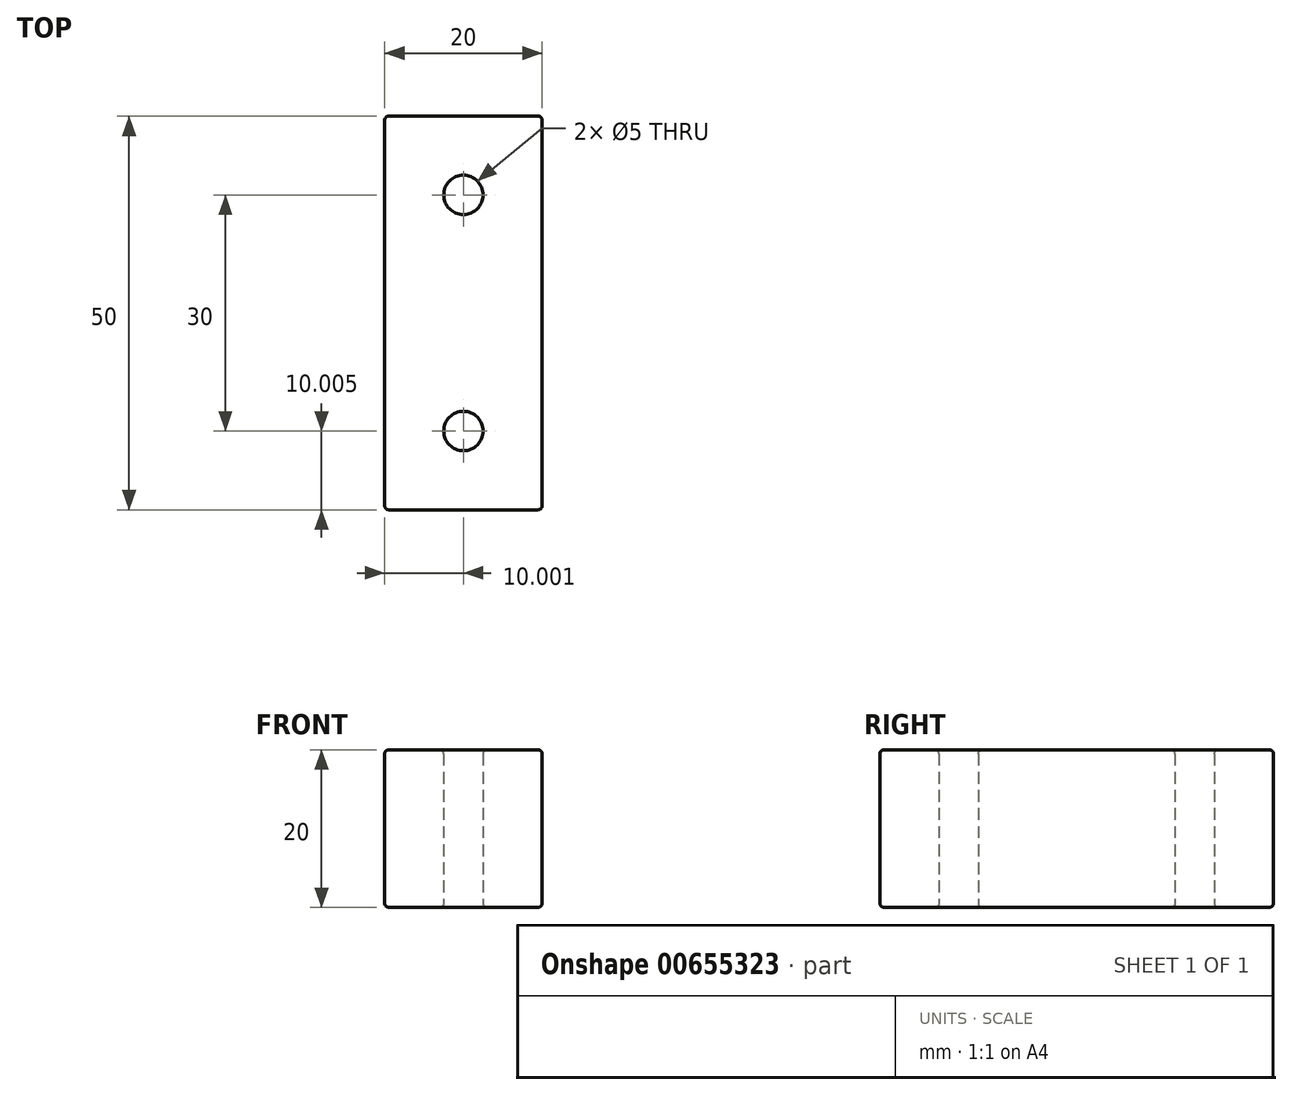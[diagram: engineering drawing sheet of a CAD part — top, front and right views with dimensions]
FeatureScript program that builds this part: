
annotation { "Feature Type Name" : "Feature", "Feature Type Description" : "" }
export const myFeature = defineFeature(function(context is Context, id is Id, definition is map)
    precondition{}
    {
        {
            var Q0;
            Q0=qCreatedBy(makeId("Top.planeOp"),FACE);
            var sketch = newSketch(context, id + "F0", { "sketchPlane" : qUnion([Q0])});
            skLineSegment(sketch, "E0.bottom", {"start": v(-44.28, 30.56) * mm, "end": v(-24.28, 30.56) * mm});
            skLineSegment(sketch, "E0.top", {"start": v(-44.28, -19.44) * mm, "end": v(-24.28, -19.44) * mm});
            skLineSegment(sketch, "E0.left", {"start": v(-44.28, 30.56) * mm, "end": v(-44.28, -19.44) * mm});
            skLineSegment(sketch, "E0.right", {"start": v(-24.28, 30.56) * mm, "end": v(-24.28, -19.44) * mm});
            skCircle(sketch, "E1", {"center": v(-34.28, 20.56) * mm, "radius": 2.5 * mm});
            skCircle(sketch, "E2", {"center": v(-34.28, -9.44) * mm, "radius": 2.5 * mm});
            skSolve(sketch);
        }
        {
            var Q0;
            Q0=makeQuery(id+"F0.imprint","IMPRINT",FACE,{"disambiguationData":[TD([[makeQuery(id+"F0.imprint","IMPRINT",EDGE,{"derivedFrom":sQuery(id+"F0.wireOp",EDGE,"E0.bottom")}),-1.0]])]});
            extrude(context, id + "F1", {"entities" : qUnion([Q0]), "depth" : 20 * mm, "offsetDistance" : 25.4 * mm});
        }
        {
            var Q0;
            Q0=makeQuery(id+"F1.opExtrude","CAP_EDGE",EDGE,{"disambiguationData":[OSD([sQuery(id+"F0.wireOp",EDGE,"E1")])],"isStart":false});
            fillet(context, id + "F2", {"entities" : qUnion([Q0]), "radius" : 0.5 * mm, "tangentPropagation" : true, "allowEdgeOverflow" : false});
        }
        {
            var Q0;
            Q0=makeQuery(id+"F1.opExtrude","SWEPT_FACE",FACE,{"disambiguationData":[OSD([sQuery(id+"F0.wireOp",EDGE,"E2")])]});
            fillet(context, id + "F3", {"entities" : qUnion([Q0]), "radius" : 0.5 * mm, "tangentPropagation" : true, "allowEdgeOverflow" : false});
        }
        {
            var Q0;
            Q0=makeQuery(id+"F1.opExtrude","CAP_EDGE",EDGE,{"disambiguationData":[OSD([sQuery(id+"F0.wireOp",EDGE,"E1")])],"isStart":true});
            fillet(context, id + "F4", {"entities" : qUnion([Q0]), "radius" : 0.5 * mm, "tangentPropagation" : true, "allowEdgeOverflow" : false});
        }
        {
            var Q0;
            Q0=makeQuery(id+"F1.opExtrude","SWEPT_EDGE",EDGE,{"disambiguationData":[OSD([sQuery(id+"F0.wireOp",EDGE,"E0.top"),sQuery(id+"F0.wireOp",EDGE,"E0.left")])]});
            var Q1;
            Q1=makeQuery(id+"F1.opExtrude","CAP_FACE",FACE,{"disambiguationData":[OSD([sQuery(id+"F0.wireOp",EDGE,"E0.bottom"),sQuery(id+"F0.wireOp",EDGE,"E0.top"),sQuery(id+"F0.wireOp",EDGE,"E0.left"),sQuery(id+"F0.wireOp",EDGE,"E0.right"),sQuery(id+"F0.wireOp",EDGE,"E1"),sQuery(id+"F0.wireOp",EDGE,"E2")])],"isStart":true});
            var Q2;
            Q2=makeQuery(id+"F1.opExtrude","SWEPT_FACE",FACE,{"disambiguationData":[OSD([sQuery(id+"F0.wireOp",EDGE,"E0.bottom")])]});
            var Q3;
            Q3=makeQuery(id+"F1.opExtrude","SWEPT_FACE",FACE,{"disambiguationData":[OSD([sQuery(id+"F0.wireOp",EDGE,"E0.left")])]});
            var Q4;
            Q4=makeQuery(id+"F1.opExtrude","CAP_FACE",FACE,{"disambiguationData":[OSD([sQuery(id+"F0.wireOp",EDGE,"E0.bottom"),sQuery(id+"F0.wireOp",EDGE,"E0.top"),sQuery(id+"F0.wireOp",EDGE,"E0.left"),sQuery(id+"F0.wireOp",EDGE,"E0.right"),sQuery(id+"F0.wireOp",EDGE,"E1"),sQuery(id+"F0.wireOp",EDGE,"E2")])],"isStart":false});
            var Q5;
            Q5=makeQuery(id+"F1.opExtrude","CAP_EDGE",EDGE,{"disambiguationData":[OSD([sQuery(id+"F0.wireOp",EDGE,"E0.left")])],"isStart":false});
            var Q6;
            Q6=makeQuery(id+"F1.opExtrude","CAP_EDGE",EDGE,{"disambiguationData":[OSD([sQuery(id+"F0.wireOp",EDGE,"E0.right")])],"isStart":true});
            var Q7;
            Q7=makeQuery(id+"F1.opExtrude","CAP_EDGE",EDGE,{"disambiguationData":[OSD([sQuery(id+"F0.wireOp",EDGE,"E0.top")])],"isStart":false});
            var Q8;
            Q8=makeQuery(id+"F1.opExtrude","SWEPT_EDGE",EDGE,{"disambiguationData":[OSD([sQuery(id+"F0.wireOp",EDGE,"E0.top"),sQuery(id+"F0.wireOp",EDGE,"E0.right")])]});
            var Q9;
            {var subQ0=sQuery(id+"F0.wireOp",EDGE,"E1");Q9=makeQuery(id+"F2.opFillet","BLEND_EDGE",EDGE,{"blendedFrom":[makeQuery(id+"F1.opExtrude","CAP_EDGE",EDGE,{"disambiguationData":[OSD([subQ0])],"isStart":false}),makeQuery(id+"F1.opExtrude","CAP_FACE",FACE,{"disambiguationData":[OSD([sQuery(id+"F0.wireOp",EDGE,"E0.bottom"),sQuery(id+"F0.wireOp",EDGE,"E0.top"),sQuery(id+"F0.wireOp",EDGE,"E0.left"),sQuery(id+"F0.wireOp",EDGE,"E0.right"),subQ0,sQuery(id+"F0.wireOp",EDGE,"E2")])],"isStart":false})],"blendedInto":[makeQuery(id+"F1.opExtrude","CAP_FACE",FACE,{"disambiguationData":[OSD([sQuery(id+"F0.wireOp",EDGE,"E0.bottom"),sQuery(id+"F0.wireOp",EDGE,"E0.top"),sQuery(id+"F0.wireOp",EDGE,"E0.left"),sQuery(id+"F0.wireOp",EDGE,"E0.right"),subQ0,sQuery(id+"F0.wireOp",EDGE,"E2")])],"isStart":false})]});}
            var Q10;
            Q10=makeQuery(id+"F1.opExtrude","SWEPT_EDGE",EDGE,{"disambiguationData":[OSD([sQuery(id+"F0.wireOp",EDGE,"E0.bottom"),sQuery(id+"F0.wireOp",EDGE,"E0.right")])]});
            var Q11;
            Q11=makeQuery(id+"F1.opExtrude","SWEPT_EDGE",EDGE,{"disambiguationData":[OSD([sQuery(id+"F0.wireOp",EDGE,"E0.bottom"),sQuery(id+"F0.wireOp",EDGE,"E0.left")])]});
            var Q12;
            {var subQ0=sQuery(id+"F0.wireOp",EDGE,"E2");Q12=makeQuery(id+"F3.opFillet","BLEND_EDGE",EDGE,{"blendedFrom":[makeQuery(id+"F1.opExtrude","CAP_EDGE",EDGE,{"disambiguationData":[OSD([subQ0])],"isStart":false}),makeQuery(id+"F1.opExtrude","CAP_FACE",FACE,{"disambiguationData":[OSD([sQuery(id+"F0.wireOp",EDGE,"E0.bottom"),sQuery(id+"F0.wireOp",EDGE,"E0.top"),sQuery(id+"F0.wireOp",EDGE,"E0.left"),sQuery(id+"F0.wireOp",EDGE,"E0.right"),sQuery(id+"F0.wireOp",EDGE,"E1"),subQ0])],"isStart":false})],"blendedInto":[makeQuery(id+"F1.opExtrude","CAP_FACE",FACE,{"disambiguationData":[OSD([sQuery(id+"F0.wireOp",EDGE,"E0.bottom"),sQuery(id+"F0.wireOp",EDGE,"E0.top"),sQuery(id+"F0.wireOp",EDGE,"E0.left"),sQuery(id+"F0.wireOp",EDGE,"E0.right"),sQuery(id+"F0.wireOp",EDGE,"E1"),subQ0])],"isStart":false})]});}
            var Q13;
            Q13=makeQuery(id+"F1.opExtrude","CAP_EDGE",EDGE,{"disambiguationData":[OSD([sQuery(id+"F0.wireOp",EDGE,"E0.left")])],"isStart":true});
            var Q14;
            Q14=makeQuery(id+"F1.opExtrude","CAP_EDGE",EDGE,{"disambiguationData":[OSD([sQuery(id+"F0.wireOp",EDGE,"E0.right")])],"isStart":false});
            var Q15;
            {var subQ0=sQuery(id+"F0.wireOp",EDGE,"E2");Q15=makeQuery(id+"F3.opFillet","BLEND_EDGE",EDGE,{"blendedFrom":[makeQuery(id+"F1.opExtrude","CAP_EDGE",EDGE,{"disambiguationData":[OSD([subQ0])],"isStart":true}),makeQuery(id+"F1.opExtrude","CAP_FACE",FACE,{"disambiguationData":[OSD([sQuery(id+"F0.wireOp",EDGE,"E0.bottom"),sQuery(id+"F0.wireOp",EDGE,"E0.top"),sQuery(id+"F0.wireOp",EDGE,"E0.left"),sQuery(id+"F0.wireOp",EDGE,"E0.right"),sQuery(id+"F0.wireOp",EDGE,"E1"),subQ0])],"isStart":true})],"blendedInto":[makeQuery(id+"F1.opExtrude","CAP_FACE",FACE,{"disambiguationData":[OSD([sQuery(id+"F0.wireOp",EDGE,"E0.bottom"),sQuery(id+"F0.wireOp",EDGE,"E0.top"),sQuery(id+"F0.wireOp",EDGE,"E0.left"),sQuery(id+"F0.wireOp",EDGE,"E0.right"),sQuery(id+"F0.wireOp",EDGE,"E1"),subQ0])],"isStart":true})]});}
            var Q16;
            Q16=makeQuery(id+"F1.opExtrude","CAP_EDGE",EDGE,{"disambiguationData":[OSD([sQuery(id+"F0.wireOp",EDGE,"E0.top")])],"isStart":true});
            var Q17;
            Q17=makeQuery(id+"F1.opExtrude","CAP_EDGE",EDGE,{"disambiguationData":[OSD([sQuery(id+"F0.wireOp",EDGE,"E0.bottom")])],"isStart":false});
            var Q18;
            {var subQ0=sQuery(id+"F0.wireOp",EDGE,"E2");Q18=makeQuery(id+"F3.opFillet","BLEND_EDGE",EDGE,{"blendedFrom":[makeQuery(id+"F1.opExtrude","CAP_EDGE",EDGE,{"disambiguationData":[OSD([subQ0])],"isStart":false}),makeQuery(id+"F1.opExtrude","SWEPT_FACE",FACE,{"disambiguationData":[OSD([subQ0])]})],"blendedInto":[makeQuery(id+"F1.opExtrude","SWEPT_FACE",FACE,{"disambiguationData":[OSD([subQ0])]})]});}
            var Q19;
            {var subQ0=sQuery(id+"F0.wireOp",EDGE,"E1");Q19=makeQuery(id+"F2.opFillet","BLEND_EDGE",EDGE,{"blendedFrom":[makeQuery(id+"F1.opExtrude","CAP_EDGE",EDGE,{"disambiguationData":[OSD([subQ0])],"isStart":false}),makeQuery(id+"F1.opExtrude","SWEPT_FACE",FACE,{"disambiguationData":[OSD([subQ0])]})],"blendedInto":[makeQuery(id+"F1.opExtrude","SWEPT_FACE",FACE,{"disambiguationData":[OSD([subQ0])]})]});}
            var Q20;
            Q20=makeQuery(id+"F1.opExtrude","CAP_EDGE",EDGE,{"disambiguationData":[OSD([sQuery(id+"F0.wireOp",EDGE,"E0.bottom")])],"isStart":true});
            var Q21;
            {var subQ0=sQuery(id+"F0.wireOp",EDGE,"E1");Q21=makeQuery(id+"F4.opFillet","BLEND_EDGE",EDGE,{"blendedFrom":[makeQuery(id+"F1.opExtrude","CAP_EDGE",EDGE,{"disambiguationData":[OSD([subQ0])],"isStart":true}),makeQuery(id+"F1.opExtrude","CAP_FACE",FACE,{"disambiguationData":[OSD([sQuery(id+"F0.wireOp",EDGE,"E0.bottom"),sQuery(id+"F0.wireOp",EDGE,"E0.top"),sQuery(id+"F0.wireOp",EDGE,"E0.left"),sQuery(id+"F0.wireOp",EDGE,"E0.right"),subQ0,sQuery(id+"F0.wireOp",EDGE,"E2")])],"isStart":true})],"blendedInto":[makeQuery(id+"F1.opExtrude","CAP_FACE",FACE,{"disambiguationData":[OSD([sQuery(id+"F0.wireOp",EDGE,"E0.bottom"),sQuery(id+"F0.wireOp",EDGE,"E0.top"),sQuery(id+"F0.wireOp",EDGE,"E0.left"),sQuery(id+"F0.wireOp",EDGE,"E0.right"),subQ0,sQuery(id+"F0.wireOp",EDGE,"E2")])],"isStart":true})]});}
            var Q22;
            {var subQ0=sQuery(id+"F0.wireOp",EDGE,"E2");Q22=makeQuery(id+"F3.opFillet","BLEND_EDGE",EDGE,{"blendedFrom":[makeQuery(id+"F1.opExtrude","CAP_EDGE",EDGE,{"disambiguationData":[OSD([subQ0])],"isStart":true}),makeQuery(id+"F1.opExtrude","SWEPT_FACE",FACE,{"disambiguationData":[OSD([subQ0])]})],"blendedInto":[makeQuery(id+"F1.opExtrude","SWEPT_FACE",FACE,{"disambiguationData":[OSD([subQ0])]})]});}
            var Q23;
            {var subQ0=sQuery(id+"F0.wireOp",EDGE,"E1");Q23=makeQuery(id+"F4.opFillet","BLEND_EDGE",EDGE,{"blendedFrom":[makeQuery(id+"F1.opExtrude","CAP_EDGE",EDGE,{"disambiguationData":[OSD([subQ0])],"isStart":true}),makeQuery(id+"F1.opExtrude","SWEPT_FACE",FACE,{"disambiguationData":[OSD([subQ0])]})],"blendedInto":[makeQuery(id+"F1.opExtrude","SWEPT_FACE",FACE,{"disambiguationData":[OSD([subQ0])]})]});}
            fillet(context, id + "F5", {"entities" : qUnion([Q0, Q1, Q2, Q3, Q4, Q5, Q6, Q7, Q8, Q9, Q10, Q11, Q12, Q13, Q14, Q15, Q16, Q17, Q18, Q19, Q20, Q21, Q22, Q23]), "radius" : 0.5 * mm, "tangentPropagation" : true, "allowEdgeOverflow" : false});
        }
    });
